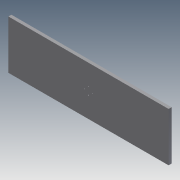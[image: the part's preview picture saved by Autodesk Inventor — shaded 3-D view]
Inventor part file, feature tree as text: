
AUTODESK INVENTOR PART (.ipt)
format: ipt  version: 2011 (Build 150239000, 239)  size: 81,920 bytes
history: native  units: in
note: dims shown in document units (in); Inventor stores cm internally (conversion verified against a paired STEP export)
features: extrude x2, sketch x2
ambient origin geometry x8: Origin, YZ Plane, XZ Plane, XY Plane, X Axis, Y Axis, Z Axis, Center Point
bodies: Solid1 (feature_tree)
feature tree (4):
  extrude  "Extrusion1"  Depth=4.0in
  extrude  "Extrusion2"  Depth=0.6299in
  sketch  "Sketch1"  dims[d0=13.14in d1=4.0in]
  sketch  "Sketch2"  dims[d2=0.25in d3=0.0in d4=0.6299in d5=0.0787in d6=0.0787in d7=0.0787in d8=0.0787in d9=0.25in d10=0.0in]
